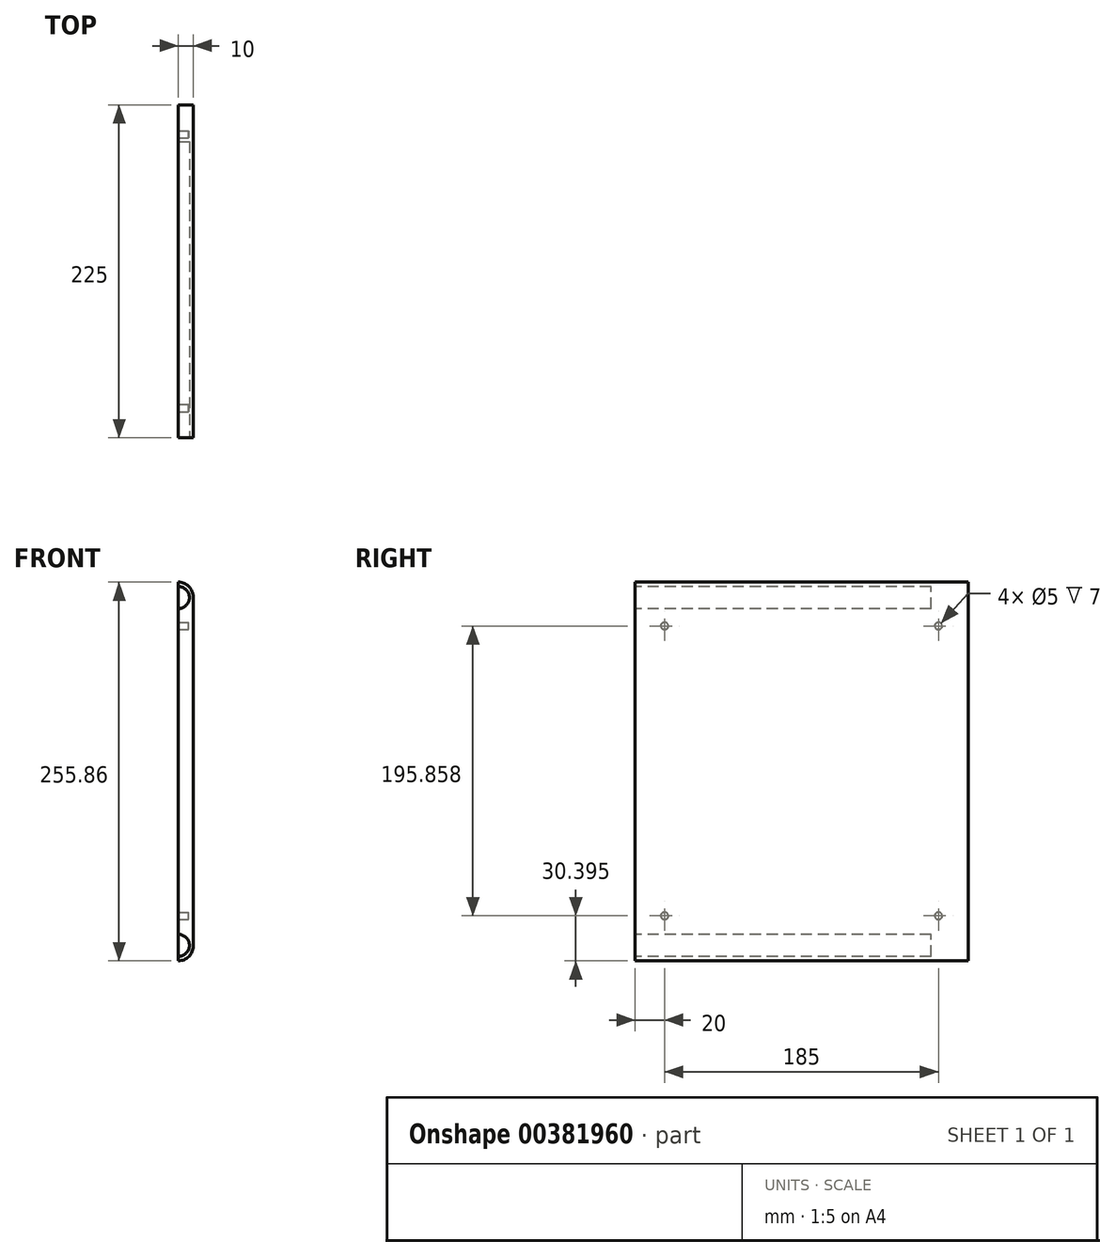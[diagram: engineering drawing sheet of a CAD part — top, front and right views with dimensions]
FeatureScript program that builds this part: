
annotation { "Feature Type Name" : "Feature", "Feature Type Description" : "" }
export const myFeature = defineFeature(function(context is Context, id is Id, definition is map)
    precondition{}
    {
        {
            var Q0;
            Q0=qCreatedBy(makeId("Front.planeOp"),FACE);
            var sketch = newSketch(context, id + "F0", { "sketchPlane" : qUnion([Q0])});
            skLineSegment(sketch, "E0.bottom", {"start": v(0, 0) * mm, "end": v(-2, 0) * mm});
            skLineSegment(sketch, "E0.top", {"start": v(0, 51.17) * mm, "end": v(-2, 51.17) * mm});
            skLineSegment(sketch, "E0.left", {"start": v(0, 0) * mm, "end": v(0, 51.17) * mm});
            skLineSegment(sketch, "E0.right", {"start": v(-2, 0) * mm, "end": v(-2, 51.17) * mm});
            skSolve(sketch);
        }
        {
            var Q0;
            Q0=makeQuery(id+"F0.imprint","IMPRINT",FACE,{"disambiguationData":[TD([[makeQuery(id+"F0.imprint","IMPRINT",EDGE,{"derivedFrom":sQuery(id+"F0.wireOp",EDGE,"E0.bottom")}),-1.0]])]});
            extrude(context, id + "F1", {"entities" : qUnion([Q0]), "depth" : 45 * mm});
        }
        {
            var Q0;
            Q0=makeQuery(id+"F1.opExtrude","SWEPT_EDGE",EDGE,{"disambiguationData":[OSD([sQuery(id+"F0.wireOp",EDGE,"E0.bottom"),sQuery(id+"F0.wireOp",EDGE,"E0.left")])]});
            var Q1;
            Q1=makeQuery(id+"F1.opExtrude","SWEPT_EDGE",EDGE,{"disambiguationData":[OSD([sQuery(id+"F0.wireOp",EDGE,"E0.top"),sQuery(id+"F0.wireOp",EDGE,"E0.left")])]});
            fillet(context, id + "F2", {"entities" : qUnion([Q0, Q1]), "radius" : 2 * mm, "tangentPropagation" : true, "allowEdgeOverflow" : false});
        }
        {
            var Q0;
            Q0=makeQuery(id+"F1.opExtrude","CAP_FACE",FACE,{"disambiguationData":[OSD([sQuery(id+"F0.wireOp",EDGE,"E0.bottom"),sQuery(id+"F0.wireOp",EDGE,"E0.top"),sQuery(id+"F0.wireOp",EDGE,"E0.left"),sQuery(id+"F0.wireOp",EDGE,"E0.right")])],"isStart":false});
            var sketch = newSketch(context, id + "F3", { "sketchPlane" : qUnion([Q0])});
            skArc(sketch, "E1", {"start": v(-2, 47.59) * mm, "mid": v(-0.5, 49.09) * mm, "end": v(-2, 50.59) * mm});
            skPoint(sketch, "E1.endSnap0", {"position": v(-0.59, 50.59) * mm});
            skArc(sketch, "E2", {"start": v(-2, 0.59) * mm, "mid": v(-0.5, 2.09) * mm, "end": v(-2, 3.59) * mm});
            skPoint(sketch, "E2.startSnap0", {"position": v(-0.59, 0.59) * mm});
            skSolve(sketch);
        }
        {
            var Q0;
            {var subQ0=sQuery(id+"F3.wireOp",EDGE,"E1");Q0=makeQuery(id+"F3.imprint","IMPRINT",FACE,{"disambiguationData":[TD([[makeQuery(id+"F3.imprint","IMPRINT",EDGE,{"derivedFrom":subQ0}),1.0]])]});}
            var Q1;
            {var subQ0=sQuery(id+"F3.wireOp",EDGE,"E2");Q1=makeQuery(id+"F3.imprint","IMPRINT",FACE,{"disambiguationData":[TD([[makeQuery(id+"F3.imprint","IMPRINT",EDGE,{"derivedFrom":subQ0}),1.0]])]});}
            extrude(context, id + "F4", {"entities" : qUnion([Q0, Q1]), "operationType" : NewBodyOperationType.REMOVE, "oppositeDirection" : true, "depth" : 40 * mm});
        }
        {
            var Q0;
            Q0=makeQuery(id+"F1.opExtrude","SWEPT_BODY",BODY,{"disambiguationData":[OSD([sQuery(id+"F0.wireOp",EDGE,"E0.bottom"),sQuery(id+"F0.wireOp",EDGE,"E0.top"),sQuery(id+"F0.wireOp",EDGE,"E0.left"),sQuery(id+"F0.wireOp",EDGE,"E0.right")])]});
            var Q1;
            Q1=qCreatedBy(makeId("Origin.pointOp"),VERTEX);
            transform(context, id + "F5", {"entities" : qUnion([Q0]), "transformType" : TransformType.SCALE_UNIFORMLY, "scale" : 5, "scalePoint" : qUnion([Q1]), "makeCopy" : false});
        }
        {
            var Q0;
            Q0=makeQuery(id+"F1.opExtrude","SWEPT_FACE",FACE,{"disambiguationData":[OSD([sQuery(id+"F0.wireOp",EDGE,"E0.left")])]});
            var sketch = newSketch(context, id + "F6", { "sketchPlane" : qUnion([Q0])});
            skCircle(sketch, "E3", {"center": v(-20, 30.4) * mm, "radius": 2.5 * mm});
            skCircle(sketch, "E4", {"center": v(-205, 30.4) * mm, "radius": 2.5 * mm});
            skCircle(sketch, "E5", {"center": v(-20, 226.25) * mm, "radius": 2.5 * mm});
            skCircle(sketch, "E6", {"center": v(-205, 226.25) * mm, "radius": 2.5 * mm});
            skSolve(sketch);
        }
        {
            var Q0;
            Q0=makeQuery(id+"F6.imprint","IMPRINT",FACE,{"disambiguationData":[TD([[makeQuery(id+"F6.imprint","IMPRINT",EDGE,{"derivedFrom":sQuery(id+"F6.wireOp",EDGE,"E6")}),1.0]])]});
            var Q1;
            Q1=makeQuery(id+"F6.imprint","IMPRINT",FACE,{"disambiguationData":[TD([[makeQuery(id+"F6.imprint","IMPRINT",EDGE,{"derivedFrom":sQuery(id+"F6.wireOp",EDGE,"E5")}),1.0]])]});
            var Q2;
            Q2=makeQuery(id+"F6.imprint","IMPRINT",FACE,{"disambiguationData":[TD([[makeQuery(id+"F6.imprint","IMPRINT",EDGE,{"derivedFrom":sQuery(id+"F6.wireOp",EDGE,"E3")}),1.0]])]});
            var Q3;
            Q3=makeQuery(id+"F6.imprint","IMPRINT",FACE,{"disambiguationData":[TD([[makeQuery(id+"F6.imprint","IMPRINT",EDGE,{"derivedFrom":sQuery(id+"F6.wireOp",EDGE,"E4")}),1.0]])]});
            extrude(context, id + "F7", {"entities" : qUnion([Q0, Q1, Q2, Q3]), "operationType" : NewBodyOperationType.REMOVE, "endBound" : BoundingType.THROUGH_ALL, "oppositeDirection" : true, "depth" : 25 * mm});
        }
        {
            var Q0;
            Q0=makeQuery(id+"F6.imprint","IMPRINT",FACE,{"disambiguationData":[TD([[makeQuery(id+"F6.imprint","IMPRINT",EDGE,{"derivedFrom":sQuery(id+"F6.wireOp",EDGE,"E3")}),-1.0]])]});
            var sketch = newSketch(context, id + "F8", { "sketchPlane" : qUnion([Q0])});
            skCircle(sketch, "E7", {"center": v(-20, 30.4) * mm, "radius": 2.5 * mm});
            skCircle(sketch, "E8", {"center": v(-205, 30.4) * mm, "radius": 2.5 * mm});
            skCircle(sketch, "E9", {"center": v(-20, 226.25) * mm, "radius": 2.5 * mm});
            skCircle(sketch, "E10", {"center": v(-205, 226.25) * mm, "radius": 2.5 * mm});
            skSolve(sketch);
        }
        {
            var Q0;
            Q0 = qSketchRegion(id + "F8", true);
            extrude(context, id + "F9", {"entities" : qUnion([Q0]), "operationType" : NewBodyOperationType.ADD, "oppositeDirection" : true, "depth" : 3 * mm});
        }
    });
